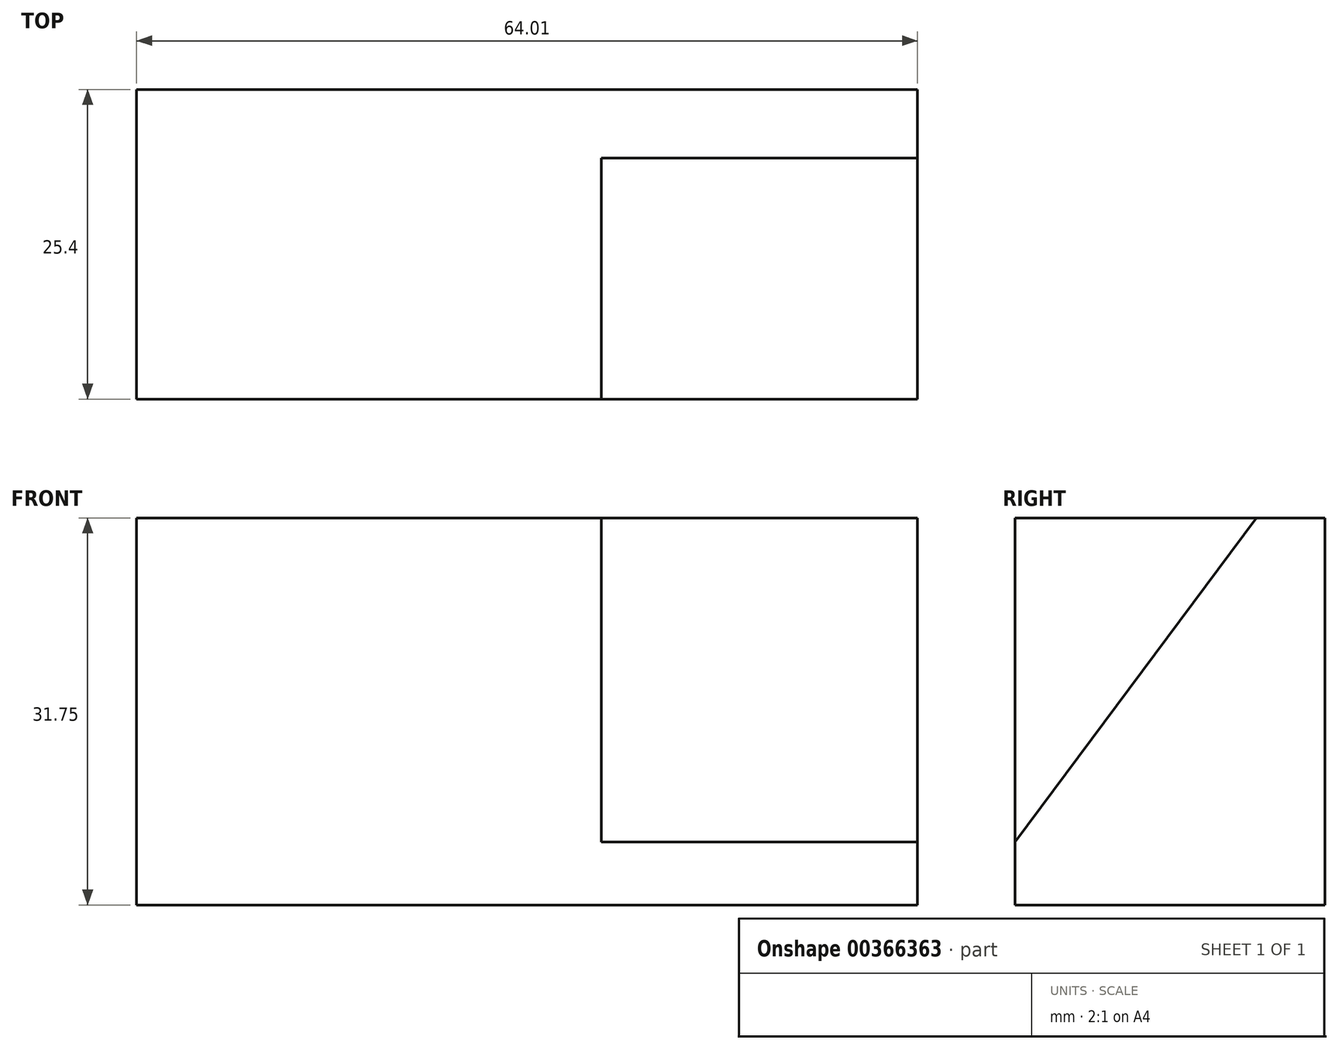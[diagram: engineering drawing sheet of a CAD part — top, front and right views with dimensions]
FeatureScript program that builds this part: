
annotation { "Feature Type Name" : "Feature", "Feature Type Description" : "" }
export const myFeature = defineFeature(function(context is Context, id is Id, definition is map)
    precondition{}
    {
        {
            var Q0;
            Q0=qCreatedBy(makeId("Right.planeOp"),FACE);
            var sketch = newSketch(context, id + "F0", { "sketchPlane" : qUnion([Q0])});
            skLineSegment(sketch, "E0", {"start": v(0, 0) * mm, "end": v(0, 31.75) * mm});
            skLineSegment(sketch, "E1", {"start": v(0, 31.75) * mm, "end": v(25.4, 31.75) * mm});
            skLineSegment(sketch, "E2", {"start": v(25.4, 31.75) * mm, "end": v(25.4, 0) * mm});
            skLineSegment(sketch, "E3", {"start": v(25.4, 0) * mm, "end": v(0, 0) * mm});
            skSolve(sketch);
        }
        {
            var Q0;
            Q0=makeQuery(id+"F0.imprint","IMPRINT",FACE,{"disambiguationData":[TD([[makeQuery(id+"F0.imprint","IMPRINT",EDGE,{"derivedFrom":sQuery(id+"F0.wireOp",EDGE,"E0")}),-1.0]])]});
            extrude(context, id + "F1", {"entities" : qUnion([Q0]), "depth" : 38.1 * mm});
        }
        {
            var Q0;
            Q0=makeQuery(id+"F1.opExtrude","CAP_FACE",FACE,{"disambiguationData":[OSD([sQuery(id+"F0.wireOp",EDGE,"E0"),sQuery(id+"F0.wireOp",EDGE,"E1"),sQuery(id+"F0.wireOp",EDGE,"E2"),sQuery(id+"F0.wireOp",EDGE,"E3")])],"isStart":false});
            var sketch = newSketch(context, id + "F2", { "sketchPlane" : qUnion([Q0])});
            skLineSegment(sketch, "E4", {"start": v(19.76, 31.75) * mm, "end": v(0, 5.15) * mm});
            skSolve(sketch);
        }
        {
            var Q0;
            {var subQ2=sQuery(id+"F2.wireOp",EDGE,"E4");Q0=makeQuery(id+"F2.imprint","IMPRINT",FACE,{"disambiguationData":[TD([[makeQuery(id+"F2.imprint","IMPRINT",EDGE,{"derivedFrom":subQ2}),1.0]])]});}
            extrude(context, id + "F3", {"entities" : qUnion([Q0]), "operationType" : NewBodyOperationType.ADD, "depth" : 25.9 * mm});
        }
    });
